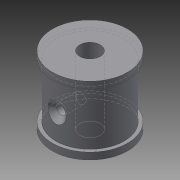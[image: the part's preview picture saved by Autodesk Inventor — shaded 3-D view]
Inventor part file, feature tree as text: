
AUTODESK INVENTOR PART (.ipt)
format: ipt  version: 2015 (Build 190159000, 159)  size: 117,248 bytes
history: native  units: mm
features: sketch x6, extrude x5, hole x1
ambient origin geometry x8: Origin, YZ Plane, XZ Plane, XY Plane, X Axis, Y Axis, Z Axis, Center Point
bodies: Solid1 (feature_tree)
feature tree (12):
  extrude  "Extrusion1"  Depth=20.0mm TaperAngle=0.0deg
  extrude  "Extrusion2"  Depth=2.0mm TaperAngle=0.0deg
  extrude  "Extrusion3"  Depth=3.0mm
  extrude  "Extrusion4"  Depth=10.0mm
  hole  "Hole1"  [1 undecoded]
  extrude  "Extrusion5"  [1 undecoded]
  sketch  "Sketch1"  dims[d0=20.0mm d1=20.0mm d2=0.0mm]
  sketch  "Sketch2"  dims[d3=22.0mm d4=2.0mm d5=0.0mm]
  sketch  "Sketch3"  dims[d6=2.0mm d7=0.0mm d8=3.0mm]
  sketch  "Sketch4"  dims[d9=10.0mm d10=0.0mm]
  sketch  "Sketch5"  dims[d11=3.0mm d12=6.0mm d13=6.0mm d14=2.0mm d15=90.0deg d16=10.0mm d17=20.594885mm d18=6.0mm]
  sketch  "Sketch6"  dims[d19=20.0mm d20=0.0mm]
note: 2 required parameter values undecoded (feature->parameter linkage not recoverable at this tier; creation-order binding heuristic only, values carry confidence <= 0.55)
